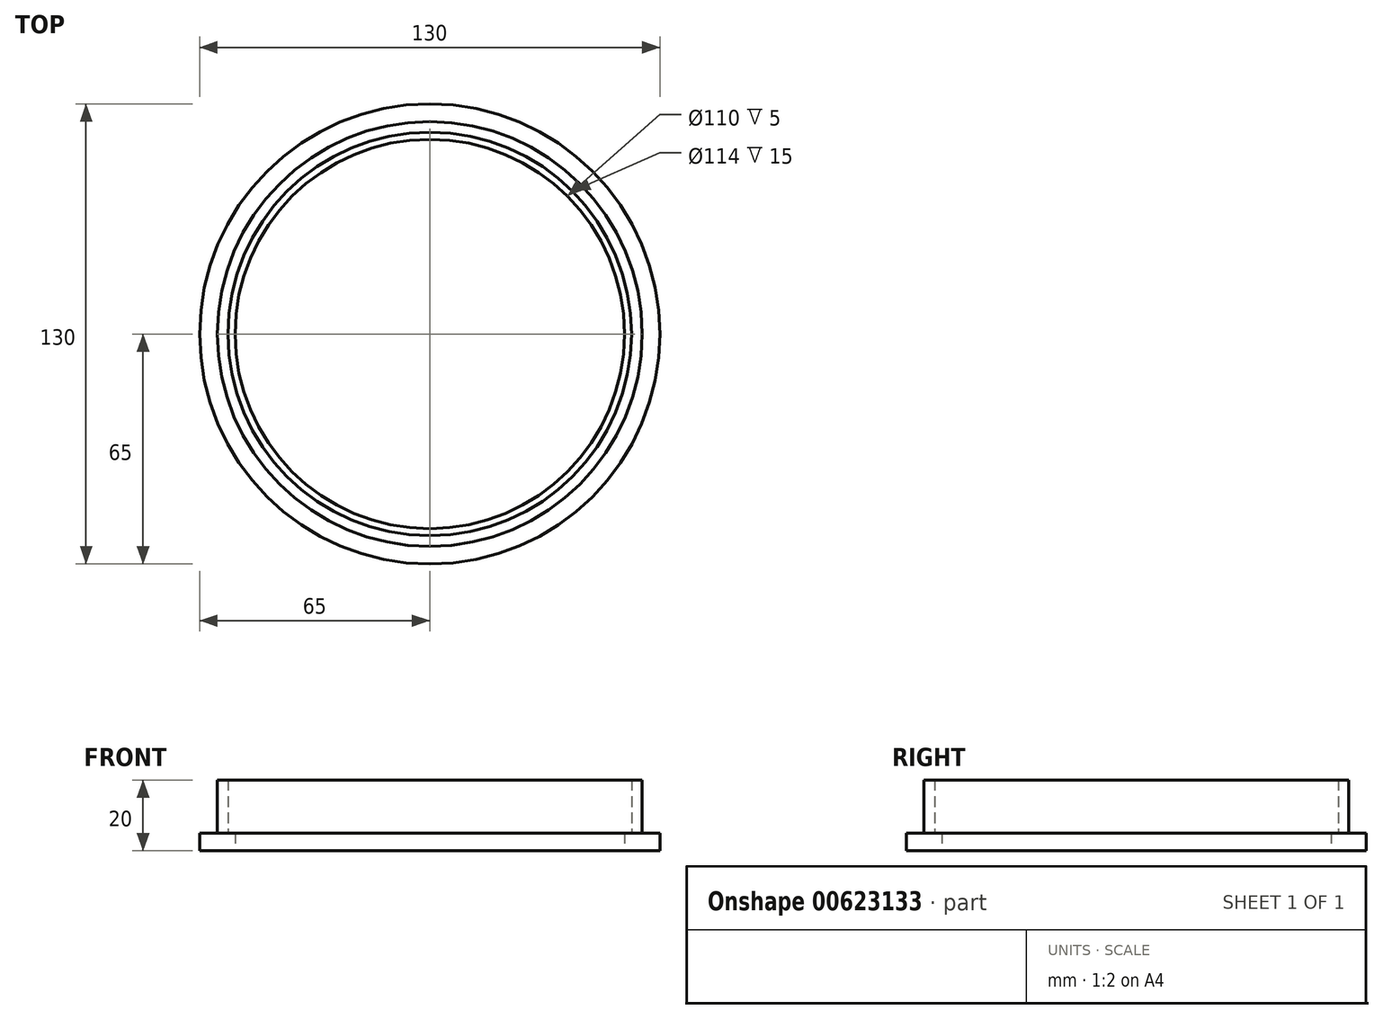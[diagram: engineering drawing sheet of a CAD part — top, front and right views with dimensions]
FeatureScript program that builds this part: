
annotation { "Feature Type Name" : "Feature", "Feature Type Description" : "" }
export const myFeature = defineFeature(function(context is Context, id is Id, definition is map)
    precondition{}
    {
        {
            var Q0;
            Q0=qCreatedBy(makeId("Front.planeOp"),FACE);
            var sketch = newSketch(context, id + "F0", { "sketchPlane" : qUnion([Q0])});
            skLineSegment(sketch, "E0", {"start": v(-65, 0) * mm, "end": v(-65, 5) * mm});
            skLineSegment(sketch, "E1", {"start": v(-65, 5) * mm, "end": v(-60, 5) * mm});
            skLineSegment(sketch, "E2", {"start": v(-60, 5) * mm, "end": v(-60, 20) * mm});
            skLineSegment(sketch, "E3", {"start": v(-60, 20) * mm, "end": v(-57, 20) * mm});
            skLineSegment(sketch, "E4", {"start": v(-57, 20) * mm, "end": v(-57, 5) * mm});
            skLineSegment(sketch, "E5", {"start": v(-57, 5) * mm, "end": v(-55, 5) * mm});
            skLineSegment(sketch, "E6", {"start": v(-55, 5) * mm, "end": v(-55, 0) * mm});
            skLineSegment(sketch, "E7", {"start": v(-55, 0) * mm, "end": v(-65, 0) * mm});
            skLineSegment(sketch, "E8", {"start": v(0, 0) * mm, "end": v(0, 30.13) * mm, "construction": true});
            skSolve(sketch);
        }
        {
            var Q0;
            Q0 = qSketchRegion(id + "F0", true);
            var Q1;
            Q1=sQuery(id+"F0.wireOp",EDGE,"E8");
            revolve(context, id + "F1", {"entities" : qUnion([Q0]), "axis" : qUnion([Q1]), "revolveType" : RevolveType.FULL});
        }
    });
